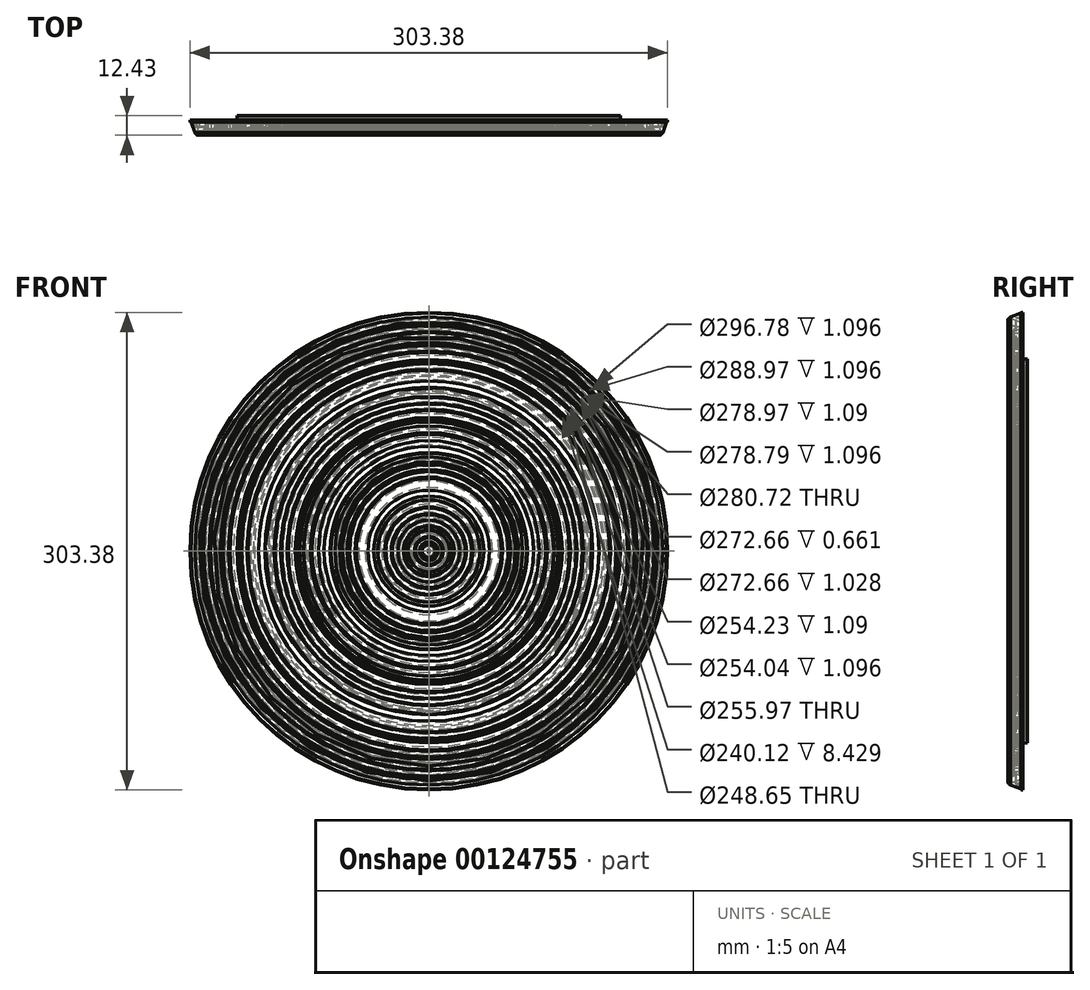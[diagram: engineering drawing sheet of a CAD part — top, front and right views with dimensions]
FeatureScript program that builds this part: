
annotation { "Feature Type Name" : "Feature", "Feature Type Description" : "" }
export const myFeature = defineFeature(function(context is Context, id is Id, definition is map)
    precondition{}
    {
        {
            var Q0;
            Q0=qCreatedBy(makeId("Top.planeOp"),FACE);
            var sketch = newSketch(context, id + "F0", { "sketchPlane" : qUnion([Q0])});
            skText(sketch, "E0", { "text": "Rapid City Public Library", "fontName": "RobotoSlab-Bold.ttf"});
            const initialGuessF0  = {"E0": [-0.07614, -0.00525, 1, 0, 0.00918]};
            skSetInitialGuess(sketch, initialGuessF0);
            skSolve(sketch);
        }
        {
            var Q0;
            Q0 = qSketchRegion(id + "F0", true);
            var Q1;
            Q1=sQuery(id+"F0.wireOp",EDGE,"E0.sketch_text.left");
            revolve(context, id + "F1", {"entities" : qUnion([Q0]), "axis" : qUnion([Q1]), "revolveType" : RevolveType.FULL});
        }
    });
